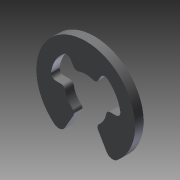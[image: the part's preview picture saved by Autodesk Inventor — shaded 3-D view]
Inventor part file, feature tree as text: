
AUTODESK INVENTOR PART (.ipt)
format: ipt  version: 2012 (Build 160160000, 160)  size: 116,224 bytes
history: native  units: in
note: dims shown in document units (in); Inventor stores cm internally (conversion verified against a paired STEP export)
features: other x7, extrude x1, sketch x1
ambient origin geometry x8: Origin, YZ Plane, XZ Plane, XY Plane, X Axis, Y Axis, Z Axis, Center Point
bodies: Solid1 (feature_tree)
feature tree (9):
  extrude  "Extrusion1"  [1 undecoded]
  other  "RR_XY"
  other  "RR_YZ"
  other  "RR_ZX"
  other  "RR_X"
  other  "RR_Y"
  other  "RR_Z"
  other  "RR_Center"
  sketch  "Sketch_1"  dims[d0=0.0435in d1=0.0in]
note: 1 required parameter value undecoded (feature->parameter linkage not recoverable at this tier; creation-order binding heuristic only, values carry confidence <= 0.55)
